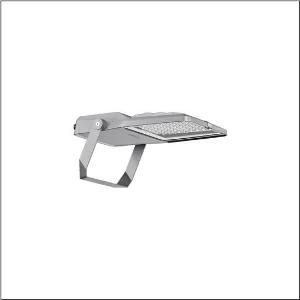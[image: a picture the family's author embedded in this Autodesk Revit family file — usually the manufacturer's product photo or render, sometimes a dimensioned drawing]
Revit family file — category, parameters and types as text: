
# Revit family: floodlight_fl_21_mini___pl64_5xa7776b2e1a_6c25
name_source: partatom
category: Lighting Fixtures
units: mm (PartAtom-declared; Revit-internal decimal feet)

## family parameters
Cut with Voids When Loaded = No
Host = Face
Light Source = No
Part Type = Normal
Room Calculation Point = No
Round Connector Dimension = Use Diameter
Shared = No

## types (1)
- --- (1 x LED, 6010 lm, 45.7 W, 3000K)
    Apparent Load = 46 VA
    CIE Flux Codes = 28 80 98 100 100
    Color Rendering = 70
    Color Temperature = 3000K
    Default Elevation = 1800 mm
    Description = Floodlight FL 21 mini, floodlight, primary light control with lens, of PMMA, primary optical cover: protective disc, of toughened safety glass, transparent, light distribution: PL64, light emission: direct distribution, installation type: surface-mounted, LED, High Power LED, rated luminous flux: 6.010lm, luminous efficacy: 132lm/W, light colour: 730, colour temperature: 3000K, control: flexible luminous flux parameterisation, time-dependent luminous flux control, constant luminous flux control, overheat protection, presetting dimming logarithmic, with terminal, 6-pole, mains connection: 220..240V, AC, 50/60Hz, start of lifetime: 46W, end of service life: 48W, reduction: 22W, luminaire housing, of diecast aluminium, powder-coated, Siteco® metallic grey (DB 702S), corrosivity category C5 mid according to DIN EN ISO 12944, sealing non-destructively replaceable, mounting bracket, of steel, galvanised, powder-coated, Siteco® metallic grey (DB 702S), Smart Interface below and above, protection rating (complete): IP66, insulation class (complete): insulation class II (safety insulation), certification: CE, ENEC, VDE, protection symbol: D, impact resistance: IK08, permissible operating ambient temperature: -40..+40°C, permissible operating ambient temperature for outdoor applications: -40..+50°C, standard: DIN EN 12944, LABS conformity tested according to VDMA 24364:2018-05, packaging unit: 1 piece

Light Distribution: PL64
    Height = 70 mm
    Lamp = 1 x LED
    Lamp Light Flux = 6010 lm
    Lamp Power = 45.7 W
    Lamp count = 1
    Length = 485 mm
    Luminous efficacy = 132 lm/W
    Manufacturer = Siteco
    ModVariant = No
    Model = 5XA7776B2E1A
    Number of Poles = 1
    OnlyDefault = Yes
    Power Factor = 1
    Product Name = Floodlight FL 21 mini | PL64
    Product group = floodlight | pylon annexe
    ProductGroupID = 6200
    Protection Class = Protection class II
    Protection Degree = IP 66
    RLX_Detail_Level = 1
    RLX_Emergency_Light_Flux = 0 lm
    RLX_Emergency_Type = 0
    RLX_Emergency_Type_DB = No
    RlxData = <blob elided: 95941 chars, md5=37330a43>
    Socket = socket
    Standby Power = 0 W
    System Light Flux = 6010 lm
    System Power = 46 W
    Type Comments = factory setting: luminous flux: 100 % | dim-lin: 254 | 463 mA
    Type Image = l_1006845.jpg
    URL = http://relux.com
    VarID = @adj_097809
    Voltage = 0 V
    Weight = 0.00 kg
    Width = 337 mm

## geometry (parser evidence)
native form markers: Blend x4, Sweep x11
no freeform markers — native parametric forms only
